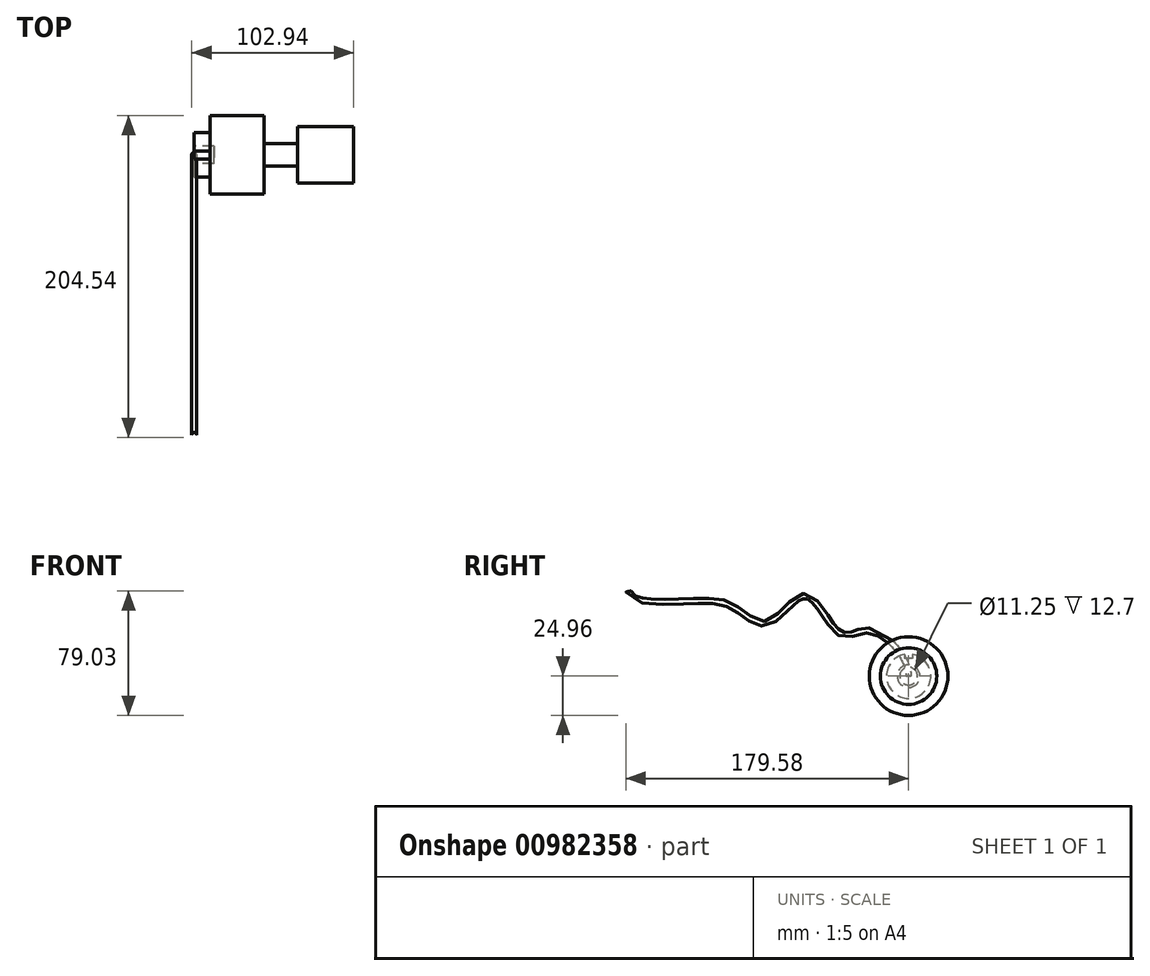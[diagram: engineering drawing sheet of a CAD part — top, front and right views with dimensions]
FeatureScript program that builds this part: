
annotation { "Feature Type Name" : "Feature", "Feature Type Description" : "" }
export const myFeature = defineFeature(function(context is Context, id is Id, definition is map)
    precondition{}
    {
        {
            var Q0;
            Q0=qCreatedBy(makeId("Front.planeOp"),FACE);
            var sketch = newSketch(context, id + "F0", { "sketchPlane" : qUnion([Q0])});
            skLineSegment(sketch, "E0", {"start": v(0, 0) * mm, "end": v(0, 14.09) * mm});
            skLineSegment(sketch, "E1", {"start": v(0, 14.09) * mm, "end": v(10.16, 14.09) * mm});
            skLineSegment(sketch, "E2", {"start": v(10.16, 14.09) * mm, "end": v(10.16, 24.96) * mm});
            skLineSegment(sketch, "E3", {"start": v(10.16, 24.96) * mm, "end": v(44.38, 24.96) * mm});
            skLineSegment(sketch, "E4", {"start": v(44.38, 24.96) * mm, "end": v(44.38, 7.25) * mm});
            skLineSegment(sketch, "E5", {"start": v(44.38, 7.25) * mm, "end": v(65.52, 7.25) * mm});
            skLineSegment(sketch, "E6", {"start": v(65.52, 7.25) * mm, "end": v(65.52, 17.91) * mm});
            skLineSegment(sketch, "E7", {"start": v(65.52, 17.91) * mm, "end": v(101.35, 17.91) * mm});
            skLineSegment(sketch, "E8", {"start": v(101.35, 17.91) * mm, "end": v(101.35, 0) * mm});
            skLineSegment(sketch, "E9", {"start": v(101.35, 0) * mm, "end": v(0, 0) * mm});
            skSolve(sketch);
        }
        {
            var Q0;
            Q0=makeQuery(id+"F0.imprint","IMPRINT",FACE,{"disambiguationData":[TD([[makeQuery(id+"F0.imprint","IMPRINT",EDGE,{"derivedFrom":sQuery(id+"F0.wireOp",EDGE,"E0")}),-1.0]])]});
            var Q1;
            Q1=sQuery(id+"F0.wireOp",EDGE,"E9");
            revolve(context, id + "F1", {"surfaceOperationType" : NewSurfaceOperationType.NEW, "entities" : qUnion([Q0]), "axis" : qUnion([Q1]), "revolveType" : RevolveType.FULL});
        }
        {
            var Q0;
            Q0=makeQuery(id+"F1.opRevolve","SWEPT_FACE",FACE,{"disambiguationData":[OSD([sQuery(id+"F0.wireOp",EDGE,"E0")])]});
            var sketch = newSketch(context, id + "F2", { "sketchPlane" : qUnion([Q0])});
            skPoint(sketch, "E10", {"position": v(0, 0) * mm});
            skSolve(sketch);
        }
        {
            var Q0;
            Q0=qCreatedBy(makeId("Right.planeOp"),FACE);
            var sketch = newSketch(context, id + "F3", { "sketchPlane" : qUnion([Q0])});
            skCircle(sketch, "E11", {"center": v(0, 0) * mm, "radius": 5.62 * mm});
            skSolve(sketch);
        }
        {
            var Q0;
            Q0 = qSketchRegion(id + "F3", true);
            extrude(context, id + "F4", {"entities" : qUnion([Q0]), "operationType" : NewBodyOperationType.REMOVE, "depth" : 12.7 * mm, "offsetDistance" : 25.4 * mm});
        }
        {
            var Q0;
            Q0=makeQuery(id+"F2.imprint","IMPRINT",FACE,{"disambiguationData":[TD([[makeQuery(id+"F2.imprint","IMPRINT",EDGE,{"derivedFrom":makeQuery(id+"F1.opRevolve","SWEPT_EDGE",EDGE,{"disambiguationData":[OSD([sQuery(id+"F0.wireOp",EDGE,"E0"),sQuery(id+"F0.wireOp",EDGE,"E1")])]})}),-1.0]])]});
            var sketch = newSketch(context, id + "F5", { "sketchPlane" : qUnion([Q0])});
            skLineSegment(sketch, "E12.bottom", {"start": v(-2.45, 14.66) * mm, "end": v(2.57, 14.66) * mm});
            skLineSegment(sketch, "E12.top", {"start": v(-2.45, 11.36) * mm, "end": v(2.57, 11.36) * mm});
            skLineSegment(sketch, "E12.left", {"start": v(-2.45, 14.66) * mm, "end": v(-2.45, 11.36) * mm});
            skLineSegment(sketch, "E12.right", {"start": v(2.57, 14.66) * mm, "end": v(2.57, 11.36) * mm});
            skSolve(sketch);
        }
        {
            var Q0;
            {var subQ0=sQuery(id+"F5.wireOp",EDGE,"E12.top");Q0=makeQuery(id+"F5.imprint","IMPRINT",FACE,{"disambiguationData":[TD([[makeQuery(id+"F5.imprint","IMPRINT",EDGE,{"derivedFrom":subQ0}),1.0]])]});}
            var Q1;
            Q1=makeQuery(id+"F1.opRevolve","SWEPT_FACE",FACE,{"disambiguationData":[OSD([sQuery(id+"F0.wireOp",EDGE,"E2")])]});
            extrude(context, id + "F6", {"entities" : qUnion([Q0]), "operationType" : NewBodyOperationType.REMOVE, "endBound" : BoundingType.UP_TO_SURFACE, "oppositeDirection" : true, "depth" : 25.4 * mm, "endBoundEntityFace" : qUnion([Q1]), "offsetDistance" : 25.4 * mm});
        }
        {
            var Q0;
            Q0=qCreatedBy(makeId("Right.planeOp"),FACE);
            var sketch = newSketch(context, id + "F7", { "sketchPlane" : qUnion([Q0])});
            skFitSpline(sketch, "E13", {"points": [v(0, 0) * mm, v(-24.44, 28.91) * mm, v(-42.97, 26.8) * mm, v(-65.2, 50.88) * mm, v(-89.1, 33.76) * mm, v(-109.12, 42.52) * mm, v(-130.76, 47.9) * mm, v(-178.02, 53.74) * mm], "startDerivative": vector(0, 219.4) * mm, "endDerivative": vector(-32.8, 155.27) * mm});
            skSolve(sketch);
        }
        {
            var Q0;
            Q0=qCreatedBy(makeId("Top.planeOp"),FACE);
            var sketch = newSketch(context, id + "F8", { "sketchPlane" : qUnion([Q0])});
            skCircle(sketch, "E14", {"center": v(0, 0) * mm, "radius": 1.59 * mm});
            skSolve(sketch);
        }
        {
            var Q0;
            Q0=makeQuery(id+"F8.imprint","IMPRINT",FACE,{"disambiguationData":[TD([[makeQuery(id+"F8.imprint","IMPRINT",EDGE,{"derivedFrom":sQuery(id+"F8.wireOp",EDGE,"E14")}),1.0]])]});
            var Q1;
            Q1=sQuery(id+"F7.wireOp",EDGE,"E13");
            sweep(context, id + "F9", {"profiles" : qUnion([Q0]), "path" : qUnion([Q1])});
        }
    });
